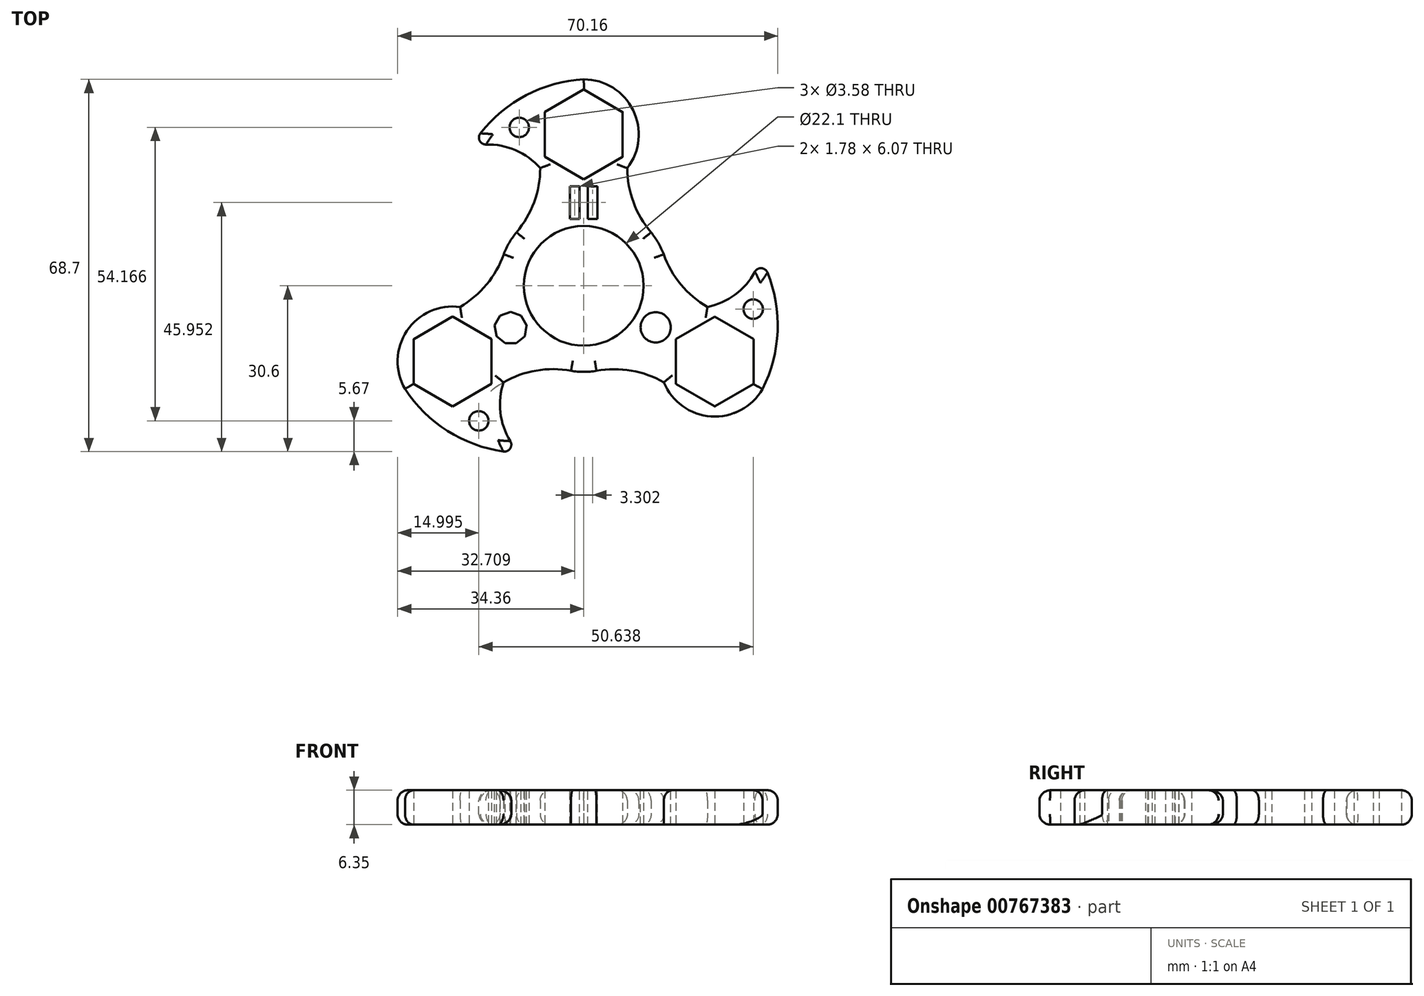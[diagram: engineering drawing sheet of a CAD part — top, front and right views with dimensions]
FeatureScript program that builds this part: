
annotation { "Feature Type Name" : "Feature", "Feature Type Description" : "" }
export const myFeature = defineFeature(function(context is Context, id is Id, definition is map)
    precondition{}
    {
        {
            var Q0;
            Q0=qCreatedBy(makeId("Top.planeOp"),FACE);
            var sketch = newSketch(context, id + "F0", { "sketchPlane" : qUnion([Q0])});
            skCircle(sketch, "E0", {"center": v(0, 0) * mm, "radius": 38.1 * mm});
            skCircle(sketch, "E1", {"center": v(0, 0) * mm, "radius": 11.05 * mm});
            skCircle(sketch, "E2.cCircle", {"center": v(0, 27.94) * mm, "radius": 8.29 * mm, "construction": true});
            skLineSegment(sketch, "E2.0", {"start": v(0, 36.23) * mm, "end": v(7.18, 32.08) * mm});
            skLineSegment(sketch, "E2.1", {"start": v(7.18, 32.08) * mm, "end": v(7.18, 23.8) * mm});
            skLineSegment(sketch, "E2.2", {"start": v(7.18, 23.8) * mm, "end": v(0, 19.65) * mm});
            skLineSegment(sketch, "E2.3", {"start": v(0, 19.65) * mm, "end": v(-7.18, 23.8) * mm});
            skLineSegment(sketch, "E2.4", {"start": v(-7.18, 23.8) * mm, "end": v(-7.18, 32.08) * mm});
            skLineSegment(sketch, "E2.5", {"start": v(-7.18, 32.08) * mm, "end": v(0, 36.23) * mm});
            skCircle(sketch, "E3", {"center": v(0, 27.94) * mm, "radius": 10.16 * mm});
            skCircle(sketch, "E4", {"center": v(0, 0) * mm, "radius": 15.88 * mm});
            skArc(sketch, "E5", {"start": v(8.04, 21.73) * mm, "mid": v(9.17, 15.41) * mm, "end": v(12.42, 9.88) * mm});
            skPoint(sketch, "E5.startSnap0", {"position": v(-3.59, 21.73) * mm});
            skArc(sketch, "E6", {"start": v(-12.42, 9.88) * mm, "mid": v(-9.16, 15.4) * mm, "end": v(-8.04, 21.73) * mm});
            skArc(sketch, "E7", {"start": v(0, 38.1) * mm, "mid": v(-11.9, 34.46) * mm, "end": v(-20.76, 25.7) * mm});
            skArc(sketch, "E8", {"start": v(-8.04, 21.73) * mm, "mid": v(-13.84, 25.5) * mm, "end": v(-20.76, 25.7) * mm});
            skCircle(sketch, "E9", {"center": v(-11.9, 29.24) * mm, "radius": 1.79 * mm});
            skArc(sketch, "E10.1.0", {"start": v(-14.8, -17.82) * mm, "mid": v(-15.16, -24.73) * mm, "end": v(-11.88, -30.83) * mm});
            skArc(sketch, "E10.1.1", {"start": v(-2.35, -15.7) * mm, "mid": v(-8.76, -15.64) * mm, "end": v(-14.8, -17.82) * mm});
            skArc(sketch, "E10.1.2", {"start": v(-33, -19.05) * mm, "mid": v(-23.89, -27.54) * mm, "end": v(-11.88, -30.83) * mm});
            skCircle(sketch, "E10.1.3", {"center": v(-24.2, -13.97) * mm, "radius": 10.16 * mm});
            skArc(sketch, "E10.1.4", {"start": v(-22.83, -3.9) * mm, "mid": v(-17.94, 0.24) * mm, "end": v(-14.77, 5.82) * mm});
            skCircle(sketch, "E10.1.5", {"center": v(-19.37, -24.93) * mm, "radius": 1.79 * mm});
            skLineSegment(sketch, "E10.1.6", {"start": v(-17.02, -18.11) * mm, "end": v(-24.2, -22.26) * mm});
            skLineSegment(sketch, "E10.1.7", {"start": v(-24.2, -22.26) * mm, "end": v(-31.37, -18.11) * mm});
            skLineSegment(sketch, "E10.1.8", {"start": v(-31.37, -18.11) * mm, "end": v(-31.37, -9.83) * mm});
            skLineSegment(sketch, "E10.1.9", {"start": v(-31.37, -9.83) * mm, "end": v(-24.2, -5.68) * mm});
            skLineSegment(sketch, "E10.1.10", {"start": v(-24.2, -5.68) * mm, "end": v(-17.02, -9.83) * mm});
            skLineSegment(sketch, "E10.1.11", {"start": v(-17.02, -9.83) * mm, "end": v(-17.02, -18.11) * mm});
            skArc(sketch, "E10.2.0", {"start": v(22.83, -3.9) * mm, "mid": v(29, -0.76) * mm, "end": v(32.64, 5.13) * mm});
            skArc(sketch, "E10.2.1", {"start": v(14.77, 5.82) * mm, "mid": v(17.93, 0.23) * mm, "end": v(22.83, -3.9) * mm});
            skArc(sketch, "E10.2.2", {"start": v(33, -19.05) * mm, "mid": v(35.8, -6.92) * mm, "end": v(32.64, 5.13) * mm});
            skCircle(sketch, "E10.2.3", {"center": v(24.2, -13.97) * mm, "radius": 10.16 * mm});
            skArc(sketch, "E10.2.4", {"start": v(14.8, -17.82) * mm, "mid": v(8.76, -15.65) * mm, "end": v(2.35, -15.7) * mm});
            skCircle(sketch, "E10.2.5", {"center": v(31.27, -4.3) * mm, "radius": 1.79 * mm});
            skLineSegment(sketch, "E10.2.6", {"start": v(24.2, -5.68) * mm, "end": v(31.37, -9.83) * mm});
            skLineSegment(sketch, "E10.2.7", {"start": v(31.37, -9.83) * mm, "end": v(31.37, -18.11) * mm});
            skLineSegment(sketch, "E10.2.8", {"start": v(31.37, -18.11) * mm, "end": v(24.2, -22.26) * mm});
            skLineSegment(sketch, "E10.2.9", {"start": v(24.2, -22.26) * mm, "end": v(17.02, -18.11) * mm});
            skLineSegment(sketch, "E10.2.10", {"start": v(17.02, -18.11) * mm, "end": v(17.02, -9.83) * mm});
            skLineSegment(sketch, "E10.2.11", {"start": v(17.02, -9.83) * mm, "end": v(24.2, -5.68) * mm});
            skSolve(sketch);
        }
        {
            var Q0;
            {var subQ0=sQuery(id+"F0.wireOp",EDGE,"E5");Q0=makeQuery(id+"F0.imprint","IMPRINT",FACE,{"disambiguationData":[TD([[makeQuery(id+"F0.imprint","IMPRINT",EDGE,{"derivedFrom":subQ0}),-1.0]])]});}
            var Q1;
            Q1=makeQuery(id+"F0.imprint","IMPRINT",FACE,{"disambiguationData":[TD([[makeQuery(id+"F0.imprint","IMPRINT",EDGE,{"derivedFrom":sQuery(id+"F0.wireOp",EDGE,"E2.0")}),1.0]])]});
            var Q2;
            {var subQ0=sQuery(id+"F0.wireOp",EDGE,"E8");Q2=makeQuery(id+"F0.imprint","IMPRINT",FACE,{"disambiguationData":[TD([[makeQuery(id+"F0.imprint","IMPRINT",EDGE,{"derivedFrom":subQ0}),-1.0]])]});}
            var Q3;
            Q3=makeQuery(id+"F0.imprint","IMPRINT",FACE,{"disambiguationData":[TD([[makeQuery(id+"F0.imprint","IMPRINT",EDGE,{"derivedFrom":sQuery(id+"F0.wireOp",EDGE,"E1")}),-1.0]])]});
            var Q4;
            Q4=makeQuery(id+"F0.imprint","IMPRINT",FACE,{"disambiguationData":[TD([[makeQuery(id+"F0.imprint","IMPRINT",EDGE,{"derivedFrom":sQuery(id+"F0.wireOp",EDGE,"E10.1.6")}),1.0]])]});
            var Q5;
            {var subQ0=sQuery(id+"F0.wireOp",EDGE,"E10.1.1");Q5=makeQuery(id+"F0.imprint","IMPRINT",FACE,{"disambiguationData":[TD([[makeQuery(id+"F0.imprint","IMPRINT",EDGE,{"derivedFrom":subQ0}),-1.0]])]});}
            var Q6;
            {var subQ1=sQuery(id+"F0.wireOp",EDGE,"E10.1.0");Q6=makeQuery(id+"F0.imprint","IMPRINT",FACE,{"disambiguationData":[TD([[makeQuery(id+"F0.imprint","IMPRINT",EDGE,{"derivedFrom":subQ1}),-1.0]])]});}
            var Q7;
            {var subQ0=sQuery(id+"F0.wireOp",EDGE,"E10.2.1");Q7=makeQuery(id+"F0.imprint","IMPRINT",FACE,{"disambiguationData":[TD([[makeQuery(id+"F0.imprint","IMPRINT",EDGE,{"derivedFrom":subQ0}),-1.0]])]});}
            var Q8;
            Q8=makeQuery(id+"F0.imprint","IMPRINT",FACE,{"disambiguationData":[TD([[makeQuery(id+"F0.imprint","IMPRINT",EDGE,{"derivedFrom":sQuery(id+"F0.wireOp",EDGE,"E10.2.6")}),1.0]])]});
            var Q9;
            {var subQ1=sQuery(id+"F0.wireOp",EDGE,"E10.2.0");Q9=makeQuery(id+"F0.imprint","IMPRINT",FACE,{"disambiguationData":[TD([[makeQuery(id+"F0.imprint","IMPRINT",EDGE,{"derivedFrom":subQ1}),-1.0]])]});}
            extrude(context, id + "F1", {"entities" : qUnion([Q0, Q1, Q2, Q3, Q4, Q5, Q6, Q7, Q8, Q9]), "depth" : 6.35 * mm, "offsetDistance" : 25.4 * mm});
        }
        {
            var Q0;
            Q0=makeQuery(id+"F1.opExtrude","SWEPT_EDGE",EDGE,{"disambiguationData":[OSD([sQuery(id+"F0.wireOp",EDGE,"E7"),sQuery(id+"F0.wireOp",EDGE,"E8")])]});
            var Q1;
            Q1=makeQuery(id+"F1.opExtrude","SWEPT_EDGE",EDGE,{"disambiguationData":[OSD([sQuery(id+"F0.wireOp",EDGE,"E10.1.0"),sQuery(id+"F0.wireOp",EDGE,"E10.1.2")])]});
            var Q2;
            Q2=makeQuery(id+"F1.opExtrude","SWEPT_EDGE",EDGE,{"disambiguationData":[OSD([sQuery(id+"F0.wireOp",EDGE,"E10.2.0"),sQuery(id+"F0.wireOp",EDGE,"E10.2.2")])]});
            fillet(context, id + "F2", {"entities" : qUnion([Q0, Q1, Q2]), "radius" : 1.27 * mm, "tangentPropagation" : true, "allowEdgeOverflow" : false});
        }
        {
            var Q0;
            {var subQ0=sQuery(id+"F0.wireOp",EDGE,"E10.1.2");var subQ1=sQuery(id+"F0.wireOp",EDGE,"E10.1.0");Q0=makeQuery(id+"F2.opFillet","BLEND_EDGE",EDGE,{"blendedFrom":[makeQuery(id+"F1.opExtrude","SWEPT_EDGE",EDGE,{"disambiguationData":[OSD([subQ1,subQ0])]}),makeQuery(id+"F1.opExtrude","CAP_FACE",FACE,{"disambiguationData":[OSD([sQuery(id+"F0.wireOp",EDGE,"E1"),sQuery(id+"F0.wireOp",EDGE,"E2.0"),sQuery(id+"F0.wireOp",EDGE,"E2.1"),sQuery(id+"F0.wireOp",EDGE,"E2.2"),sQuery(id+"F0.wireOp",EDGE,"E2.3"),sQuery(id+"F0.wireOp",EDGE,"E2.4"),sQuery(id+"F0.wireOp",EDGE,"E2.5"),sQuery(id+"F0.wireOp",EDGE,"E3"),sQuery(id+"F0.wireOp",EDGE,"E4"),sQuery(id+"F0.wireOp",EDGE,"E5"),sQuery(id+"F0.wireOp",EDGE,"E6"),sQuery(id+"F0.wireOp",EDGE,"E7"),sQuery(id+"F0.wireOp",EDGE,"E8"),sQuery(id+"F0.wireOp",EDGE,"E9"),subQ1,sQuery(id+"F0.wireOp",EDGE,"E10.1.1"),subQ0,sQuery(id+"F0.wireOp",EDGE,"E10.1.3"),sQuery(id+"F0.wireOp",EDGE,"E10.1.4"),sQuery(id+"F0.wireOp",EDGE,"E10.1.5"),sQuery(id+"F0.wireOp",EDGE,"E10.1.6"),sQuery(id+"F0.wireOp",EDGE,"E10.1.7"),sQuery(id+"F0.wireOp",EDGE,"E10.1.8"),sQuery(id+"F0.wireOp",EDGE,"E10.1.9"),sQuery(id+"F0.wireOp",EDGE,"E10.1.10"),sQuery(id+"F0.wireOp",EDGE,"E10.1.11"),sQuery(id+"F0.wireOp",EDGE,"E10.2.0"),sQuery(id+"F0.wireOp",EDGE,"E10.2.1"),sQuery(id+"F0.wireOp",EDGE,"E10.2.2"),sQuery(id+"F0.wireOp",EDGE,"E10.2.3"),sQuery(id+"F0.wireOp",EDGE,"E10.2.4"),sQuery(id+"F0.wireOp",EDGE,"E10.2.5"),sQuery(id+"F0.wireOp",EDGE,"E10.2.6"),sQuery(id+"F0.wireOp",EDGE,"E10.2.7"),sQuery(id+"F0.wireOp",EDGE,"E10.2.8"),sQuery(id+"F0.wireOp",EDGE,"E10.2.9"),sQuery(id+"F0.wireOp",EDGE,"E10.2.10"),sQuery(id+"F0.wireOp",EDGE,"E10.2.11")])],"isStart":false})],"blendedInto":[makeQuery(id+"F1.opExtrude","CAP_FACE",FACE,{"disambiguationData":[OSD([sQuery(id+"F0.wireOp",EDGE,"E1"),sQuery(id+"F0.wireOp",EDGE,"E2.0"),sQuery(id+"F0.wireOp",EDGE,"E2.1"),sQuery(id+"F0.wireOp",EDGE,"E2.2"),sQuery(id+"F0.wireOp",EDGE,"E2.3"),sQuery(id+"F0.wireOp",EDGE,"E2.4"),sQuery(id+"F0.wireOp",EDGE,"E2.5"),sQuery(id+"F0.wireOp",EDGE,"E3"),sQuery(id+"F0.wireOp",EDGE,"E4"),sQuery(id+"F0.wireOp",EDGE,"E5"),sQuery(id+"F0.wireOp",EDGE,"E6"),sQuery(id+"F0.wireOp",EDGE,"E7"),sQuery(id+"F0.wireOp",EDGE,"E8"),sQuery(id+"F0.wireOp",EDGE,"E9"),subQ1,sQuery(id+"F0.wireOp",EDGE,"E10.1.1"),subQ0,sQuery(id+"F0.wireOp",EDGE,"E10.1.3"),sQuery(id+"F0.wireOp",EDGE,"E10.1.4"),sQuery(id+"F0.wireOp",EDGE,"E10.1.5"),sQuery(id+"F0.wireOp",EDGE,"E10.1.6"),sQuery(id+"F0.wireOp",EDGE,"E10.1.7"),sQuery(id+"F0.wireOp",EDGE,"E10.1.8"),sQuery(id+"F0.wireOp",EDGE,"E10.1.9"),sQuery(id+"F0.wireOp",EDGE,"E10.1.10"),sQuery(id+"F0.wireOp",EDGE,"E10.1.11"),sQuery(id+"F0.wireOp",EDGE,"E10.2.0"),sQuery(id+"F0.wireOp",EDGE,"E10.2.1"),sQuery(id+"F0.wireOp",EDGE,"E10.2.2"),sQuery(id+"F0.wireOp",EDGE,"E10.2.3"),sQuery(id+"F0.wireOp",EDGE,"E10.2.4"),sQuery(id+"F0.wireOp",EDGE,"E10.2.5"),sQuery(id+"F0.wireOp",EDGE,"E10.2.6"),sQuery(id+"F0.wireOp",EDGE,"E10.2.7"),sQuery(id+"F0.wireOp",EDGE,"E10.2.8"),sQuery(id+"F0.wireOp",EDGE,"E10.2.9"),sQuery(id+"F0.wireOp",EDGE,"E10.2.10"),sQuery(id+"F0.wireOp",EDGE,"E10.2.11")])],"isStart":false})]});}
            var Q1;
            Q1=makeQuery(id+"F1.opExtrude","CAP_EDGE",EDGE,{"disambiguationData":[OSD([sQuery(id+"F0.wireOp",EDGE,"E10.1.1")])],"isStart":false});
            var Q2;
            Q2=makeQuery(id+"F1.opExtrude","CAP_EDGE",EDGE,{"disambiguationData":[OSD([sQuery(id+"F0.wireOp",EDGE,"E10.1.0")])],"isStart":false});
            var Q3;
            Q3=makeQuery(id+"F1.opExtrude","CAP_EDGE",EDGE,{"disambiguationData":[OSD([sQuery(id+"F0.wireOp",EDGE,"E10.2.4")])],"isStart":false});
            var Q4;
            Q4=makeQuery(id+"F1.opExtrude","CAP_EDGE",EDGE,{"disambiguationData":[OSD([sQuery(id+"F0.wireOp",EDGE,"E10.2.3")])],"isStart":false});
            var Q5;
            Q5=makeQuery(id+"F1.opExtrude","CAP_EDGE",EDGE,{"disambiguationData":[OSD([sQuery(id+"F0.wireOp",EDGE,"E10.2.2")])],"isStart":false});
            var Q6;
            Q6=makeQuery(id+"F1.opExtrude","CAP_EDGE",EDGE,{"disambiguationData":[OSD([sQuery(id+"F0.wireOp",EDGE,"E10.2.1")])],"isStart":false});
            var Q7;
            Q7=makeQuery(id+"F1.opExtrude","CAP_EDGE",EDGE,{"disambiguationData":[OSD([sQuery(id+"F0.wireOp",EDGE,"E5")])],"isStart":false});
            var Q8;
            Q8=makeQuery(id+"F1.opExtrude","CAP_EDGE",EDGE,{"disambiguationData":[OSD([sQuery(id+"F0.wireOp",EDGE,"E3")])],"isStart":false});
            var Q9;
            Q9=makeQuery(id+"F1.opExtrude","CAP_EDGE",EDGE,{"disambiguationData":[OSD([sQuery(id+"F0.wireOp",EDGE,"E7")])],"isStart":false});
            var Q10;
            Q10=makeQuery(id+"F1.opExtrude","CAP_EDGE",EDGE,{"disambiguationData":[OSD([sQuery(id+"F0.wireOp",EDGE,"E6")])],"isStart":false});
            var Q11;
            Q11=makeQuery(id+"F1.opExtrude","CAP_EDGE",EDGE,{"disambiguationData":[OSD([sQuery(id+"F0.wireOp",EDGE,"E10.1.4")])],"isStart":false});
            var Q12;
            Q12=makeQuery(id+"F1.opExtrude","CAP_EDGE",EDGE,{"disambiguationData":[OSD([sQuery(id+"F0.wireOp",EDGE,"E10.1.3")])],"isStart":false});
            var Q13;
            Q13=makeQuery(id+"F1.opExtrude","CAP_EDGE",EDGE,{"disambiguationData":[OSD([sQuery(id+"F0.wireOp",EDGE,"E10.1.4")])],"isStart":true});
            var Q14;
            Q14=makeQuery(id+"F1.opExtrude","CAP_EDGE",EDGE,{"disambiguationData":[OSD([sQuery(id+"F0.wireOp",EDGE,"E6")])],"isStart":true});
            var Q15;
            Q15=makeQuery(id+"F1.opExtrude","CAP_EDGE",EDGE,{"disambiguationData":[OSD([sQuery(id+"F0.wireOp",EDGE,"E10.1.3")])],"isStart":true});
            var Q16;
            Q16=makeQuery(id+"F1.opExtrude","CAP_EDGE",EDGE,{"disambiguationData":[OSD([sQuery(id+"F0.wireOp",EDGE,"E10.1.2")])],"isStart":true});
            var Q17;
            Q17=makeQuery(id+"F1.opExtrude","CAP_EDGE",EDGE,{"disambiguationData":[OSD([sQuery(id+"F0.wireOp",EDGE,"E7")])],"isStart":true});
            var Q18;
            {var subQ0=sQuery(id+"F0.wireOp",EDGE,"E8");var subQ1=sQuery(id+"F0.wireOp",EDGE,"E7");Q18=makeQuery(id+"F2.opFillet","BLEND_EDGE",EDGE,{"blendedFrom":[makeQuery(id+"F1.opExtrude","SWEPT_EDGE",EDGE,{"disambiguationData":[OSD([subQ1,subQ0])]}),makeQuery(id+"F1.opExtrude","CAP_FACE",FACE,{"disambiguationData":[OSD([sQuery(id+"F0.wireOp",EDGE,"E1"),sQuery(id+"F0.wireOp",EDGE,"E2.0"),sQuery(id+"F0.wireOp",EDGE,"E2.1"),sQuery(id+"F0.wireOp",EDGE,"E2.2"),sQuery(id+"F0.wireOp",EDGE,"E2.3"),sQuery(id+"F0.wireOp",EDGE,"E2.4"),sQuery(id+"F0.wireOp",EDGE,"E2.5"),sQuery(id+"F0.wireOp",EDGE,"E3"),sQuery(id+"F0.wireOp",EDGE,"E4"),sQuery(id+"F0.wireOp",EDGE,"E5"),sQuery(id+"F0.wireOp",EDGE,"E6"),subQ1,subQ0,sQuery(id+"F0.wireOp",EDGE,"E9"),sQuery(id+"F0.wireOp",EDGE,"E10.1.0"),sQuery(id+"F0.wireOp",EDGE,"E10.1.1"),sQuery(id+"F0.wireOp",EDGE,"E10.1.2"),sQuery(id+"F0.wireOp",EDGE,"E10.1.3"),sQuery(id+"F0.wireOp",EDGE,"E10.1.4"),sQuery(id+"F0.wireOp",EDGE,"E10.1.5"),sQuery(id+"F0.wireOp",EDGE,"E10.1.6"),sQuery(id+"F0.wireOp",EDGE,"E10.1.7"),sQuery(id+"F0.wireOp",EDGE,"E10.1.8"),sQuery(id+"F0.wireOp",EDGE,"E10.1.9"),sQuery(id+"F0.wireOp",EDGE,"E10.1.10"),sQuery(id+"F0.wireOp",EDGE,"E10.1.11"),sQuery(id+"F0.wireOp",EDGE,"E10.2.0"),sQuery(id+"F0.wireOp",EDGE,"E10.2.1"),sQuery(id+"F0.wireOp",EDGE,"E10.2.2"),sQuery(id+"F0.wireOp",EDGE,"E10.2.3"),sQuery(id+"F0.wireOp",EDGE,"E10.2.4"),sQuery(id+"F0.wireOp",EDGE,"E10.2.5"),sQuery(id+"F0.wireOp",EDGE,"E10.2.6"),sQuery(id+"F0.wireOp",EDGE,"E10.2.7"),sQuery(id+"F0.wireOp",EDGE,"E10.2.8"),sQuery(id+"F0.wireOp",EDGE,"E10.2.9"),sQuery(id+"F0.wireOp",EDGE,"E10.2.10"),sQuery(id+"F0.wireOp",EDGE,"E10.2.11")])],"isStart":true})],"blendedInto":[makeQuery(id+"F1.opExtrude","CAP_FACE",FACE,{"disambiguationData":[OSD([sQuery(id+"F0.wireOp",EDGE,"E1"),sQuery(id+"F0.wireOp",EDGE,"E2.0"),sQuery(id+"F0.wireOp",EDGE,"E2.1"),sQuery(id+"F0.wireOp",EDGE,"E2.2"),sQuery(id+"F0.wireOp",EDGE,"E2.3"),sQuery(id+"F0.wireOp",EDGE,"E2.4"),sQuery(id+"F0.wireOp",EDGE,"E2.5"),sQuery(id+"F0.wireOp",EDGE,"E3"),sQuery(id+"F0.wireOp",EDGE,"E4"),sQuery(id+"F0.wireOp",EDGE,"E5"),sQuery(id+"F0.wireOp",EDGE,"E6"),subQ1,subQ0,sQuery(id+"F0.wireOp",EDGE,"E9"),sQuery(id+"F0.wireOp",EDGE,"E10.1.0"),sQuery(id+"F0.wireOp",EDGE,"E10.1.1"),sQuery(id+"F0.wireOp",EDGE,"E10.1.2"),sQuery(id+"F0.wireOp",EDGE,"E10.1.3"),sQuery(id+"F0.wireOp",EDGE,"E10.1.4"),sQuery(id+"F0.wireOp",EDGE,"E10.1.5"),sQuery(id+"F0.wireOp",EDGE,"E10.1.6"),sQuery(id+"F0.wireOp",EDGE,"E10.1.7"),sQuery(id+"F0.wireOp",EDGE,"E10.1.8"),sQuery(id+"F0.wireOp",EDGE,"E10.1.9"),sQuery(id+"F0.wireOp",EDGE,"E10.1.10"),sQuery(id+"F0.wireOp",EDGE,"E10.1.11"),sQuery(id+"F0.wireOp",EDGE,"E10.2.0"),sQuery(id+"F0.wireOp",EDGE,"E10.2.1"),sQuery(id+"F0.wireOp",EDGE,"E10.2.2"),sQuery(id+"F0.wireOp",EDGE,"E10.2.3"),sQuery(id+"F0.wireOp",EDGE,"E10.2.4"),sQuery(id+"F0.wireOp",EDGE,"E10.2.5"),sQuery(id+"F0.wireOp",EDGE,"E10.2.6"),sQuery(id+"F0.wireOp",EDGE,"E10.2.7"),sQuery(id+"F0.wireOp",EDGE,"E10.2.8"),sQuery(id+"F0.wireOp",EDGE,"E10.2.9"),sQuery(id+"F0.wireOp",EDGE,"E10.2.10"),sQuery(id+"F0.wireOp",EDGE,"E10.2.11")])],"isStart":true})]});}
            var Q19;
            Q19=makeQuery(id+"F1.opExtrude","CAP_EDGE",EDGE,{"disambiguationData":[OSD([sQuery(id+"F0.wireOp",EDGE,"E3")])],"isStart":true});
            var Q20;
            Q20=makeQuery(id+"F1.opExtrude","CAP_EDGE",EDGE,{"disambiguationData":[OSD([sQuery(id+"F0.wireOp",EDGE,"E5")])],"isStart":true});
            var Q21;
            Q21=makeQuery(id+"F1.opExtrude","CAP_EDGE",EDGE,{"disambiguationData":[OSD([sQuery(id+"F0.wireOp",EDGE,"E10.2.1")])],"isStart":true});
            var Q22;
            Q22=makeQuery(id+"F1.opExtrude","CAP_EDGE",EDGE,{"disambiguationData":[OSD([sQuery(id+"F0.wireOp",EDGE,"E10.2.0")])],"isStart":true});
            fillet(context, id + "F3", {"entities" : qUnion([Q0, Q1, Q2, Q3, Q4, Q5, Q6, Q7, Q8, Q9, Q10, Q11, Q12, Q13, Q14, Q15, Q16, Q17, Q18, Q19, Q20, Q21, Q22]), "radius" : 1.9 * mm, "tangentPropagation" : true, "allowEdgeOverflow" : false});
        }
        {
            var Q0;
            Q0=makeQuery(id+"F3.opFillet","SPLIT",FACE,{"disambiguationData":[OD(6.0)],"derivedFrom":makeQuery(id+"F1.opExtrude","CAP_FACE",FACE,{"disambiguationData":[OSD([sQuery(id+"F0.wireOp",EDGE,"E1"),sQuery(id+"F0.wireOp",EDGE,"E2.0"),sQuery(id+"F0.wireOp",EDGE,"E2.1"),sQuery(id+"F0.wireOp",EDGE,"E2.2"),sQuery(id+"F0.wireOp",EDGE,"E2.3"),sQuery(id+"F0.wireOp",EDGE,"E2.4"),sQuery(id+"F0.wireOp",EDGE,"E2.5"),sQuery(id+"F0.wireOp",EDGE,"E3"),sQuery(id+"F0.wireOp",EDGE,"E4"),sQuery(id+"F0.wireOp",EDGE,"E5"),sQuery(id+"F0.wireOp",EDGE,"E6"),sQuery(id+"F0.wireOp",EDGE,"E7"),sQuery(id+"F0.wireOp",EDGE,"E8"),sQuery(id+"F0.wireOp",EDGE,"E9"),sQuery(id+"F0.wireOp",EDGE,"E10.1.0"),sQuery(id+"F0.wireOp",EDGE,"E10.1.1"),sQuery(id+"F0.wireOp",EDGE,"E10.1.2"),sQuery(id+"F0.wireOp",EDGE,"E10.1.3"),sQuery(id+"F0.wireOp",EDGE,"E10.1.4"),sQuery(id+"F0.wireOp",EDGE,"E10.1.5"),sQuery(id+"F0.wireOp",EDGE,"E10.1.6"),sQuery(id+"F0.wireOp",EDGE,"E10.1.7"),sQuery(id+"F0.wireOp",EDGE,"E10.1.8"),sQuery(id+"F0.wireOp",EDGE,"E10.1.9"),sQuery(id+"F0.wireOp",EDGE,"E10.1.10"),sQuery(id+"F0.wireOp",EDGE,"E10.1.11"),sQuery(id+"F0.wireOp",EDGE,"E10.2.0"),sQuery(id+"F0.wireOp",EDGE,"E10.2.1"),sQuery(id+"F0.wireOp",EDGE,"E10.2.2"),sQuery(id+"F0.wireOp",EDGE,"E10.2.3"),sQuery(id+"F0.wireOp",EDGE,"E10.2.4"),sQuery(id+"F0.wireOp",EDGE,"E10.2.5"),sQuery(id+"F0.wireOp",EDGE,"E10.2.6"),sQuery(id+"F0.wireOp",EDGE,"E10.2.7"),sQuery(id+"F0.wireOp",EDGE,"E10.2.8"),sQuery(id+"F0.wireOp",EDGE,"E10.2.9"),sQuery(id+"F0.wireOp",EDGE,"E10.2.10"),sQuery(id+"F0.wireOp",EDGE,"E10.2.11")])],"isStart":false})});
            var sketch = newSketch(context, id + "F4", { "sketchPlane" : qUnion([Q0])});
            skLineSegment(sketch, "E11.bottom", {"start": v(-2.54, 18.38) * mm, "end": v(-0.76, 18.38) * mm});
            skLineSegment(sketch, "E11.top", {"start": v(-2.54, 12.32) * mm, "end": v(-0.76, 12.32) * mm});
            skLineSegment(sketch, "E11.left", {"start": v(-2.54, 18.38) * mm, "end": v(-2.54, 12.32) * mm});
            skLineSegment(sketch, "E11.right", {"start": v(-0.76, 18.38) * mm, "end": v(-0.76, 12.32) * mm});
            skLineSegment(sketch, "E12.bottom", {"start": v(0.76, 18.38) * mm, "end": v(2.54, 18.38) * mm});
            skLineSegment(sketch, "E12.top", {"start": v(0.76, 12.32) * mm, "end": v(2.54, 12.32) * mm});
            skLineSegment(sketch, "E12.left", {"start": v(0.76, 18.38) * mm, "end": v(0.76, 12.32) * mm});
            skLineSegment(sketch, "E12.right", {"start": v(2.54, 18.38) * mm, "end": v(2.54, 12.32) * mm});
            skLineSegment(sketch, "E13", {"start": v(0, 19.65) * mm, "end": v(0, 11.05) * mm, "construction": true});
            skLineSegment(sketch, "E14", {"start": v(0, 19.65) * mm, "end": v(11.28, 19.65) * mm, "construction": true});
            skLineSegment(sketch, "E15", {"start": v(0, 11.05) * mm, "end": v(15.26, 11.05) * mm, "construction": true});
            skLineSegment(sketch, "E16", {"start": v(17.02, -9.83) * mm, "end": v(0, 0) * mm, "construction": true});
            skLineSegment(sketch, "E17", {"start": v(17.02, -9.83) * mm, "end": v(10.59, -20.97) * mm, "construction": true});
            skLineSegment(sketch, "E18", {"start": v(-24.2, -13.97) * mm, "end": v(0, 0) * mm, "construction": true});
            skLineSegment(sketch, "E19", {"start": v(-17.02, -9.83) * mm, "end": v(-11.61, -19.2) * mm, "construction": true});
            skCircle(sketch, "E20", {"center": v(13.28, -7.67) * mm, "radius": 2.8 * mm});
            skCircle(sketch, "E21", {"center": v(13.28, -7.67) * mm, "radius": 1.02 * mm});
            skCircle(sketch, "E22.cCircle", {"center": v(-13.5, -7.8) * mm, "radius": 2.82 * mm, "construction": true});
            skLineSegment(sketch, "E22.0", {"start": v(-16.44, -7.27) * mm, "end": v(-15.42, -5.5) * mm});
            skLineSegment(sketch, "E22.1", {"start": v(-15.42, -5.5) * mm, "end": v(-13.5, -4.8) * mm});
            skLineSegment(sketch, "E22.2", {"start": v(-13.5, -4.8) * mm, "end": v(-11.57, -5.5) * mm});
            skLineSegment(sketch, "E22.3", {"start": v(-11.57, -5.5) * mm, "end": v(-10.54, -7.27) * mm});
            skLineSegment(sketch, "E22.4", {"start": v(-10.54, -7.27) * mm, "end": v(-10.9, -9.29) * mm});
            skLineSegment(sketch, "E22.5", {"start": v(-10.9, -9.29) * mm, "end": v(-12.47, -10.6) * mm});
            skLineSegment(sketch, "E22.6", {"start": v(-12.47, -10.6) * mm, "end": v(-14.52, -10.6) * mm});
            skLineSegment(sketch, "E22.7", {"start": v(-14.52, -10.6) * mm, "end": v(-16.09, -9.29) * mm});
            skLineSegment(sketch, "E22.8", {"start": v(-16.09, -9.29) * mm, "end": v(-16.44, -7.27) * mm});
            skPoint(sketch, "E22.0.midPoint", {"position": v(-15.93, -6.38) * mm});
            skSolve(sketch);
        }
        {
            var Q0;
            Q0=makeQuery(id+"F4.imprint","IMPRINT",FACE,{"disambiguationData":[TD([[makeQuery(id+"F4.imprint","IMPRINT",EDGE,{"derivedFrom":sQuery(id+"F4.wireOp",EDGE,"E11.bottom")}),-1.0]])]});
            var Q1;
            Q1=makeQuery(id+"F4.imprint","IMPRINT",FACE,{"disambiguationData":[TD([[makeQuery(id+"F4.imprint","IMPRINT",EDGE,{"derivedFrom":sQuery(id+"F4.wireOp",EDGE,"E12.bottom")}),-1.0]])]});
            extrude(context, id + "F5", {"entities" : qUnion([Q0, Q1]), "operationType" : NewBodyOperationType.REMOVE, "oppositeDirection" : true, "depth" : 25.4 * mm, "offsetDistance" : 25.4 * mm});
        }
        {
            var Q0;
            Q0=makeQuery(id+"F4.imprint","IMPRINT",FACE,{"disambiguationData":[TD([[makeQuery(id+"F4.imprint","IMPRINT",EDGE,{"derivedFrom":sQuery(id+"F4.wireOp",EDGE,"E20")}),1.0]])]});
            var Q1;
            Q1=makeQuery(id+"F4.imprint","IMPRINT",FACE,{"disambiguationData":[TD([[makeQuery(id+"F4.imprint","IMPRINT",EDGE,{"derivedFrom":sQuery(id+"F4.wireOp",EDGE,"E21")}),1.0]])]});
            var Q2;
            Q2=makeQuery(id+"F4.imprint","IMPRINT",FACE,{"disambiguationData":[TD([[makeQuery(id+"F4.imprint","IMPRINT",EDGE,{"derivedFrom":sQuery(id+"F4.wireOp",EDGE,"E22.0")}),-1.0]])]});
            extrude(context, id + "F6", {"entities" : qUnion([Q0, Q1, Q2]), "operationType" : NewBodyOperationType.REMOVE, "oppositeDirection" : true, "depth" : 25.4 * mm, "offsetDistance" : 25.4 * mm});
        }
    });
